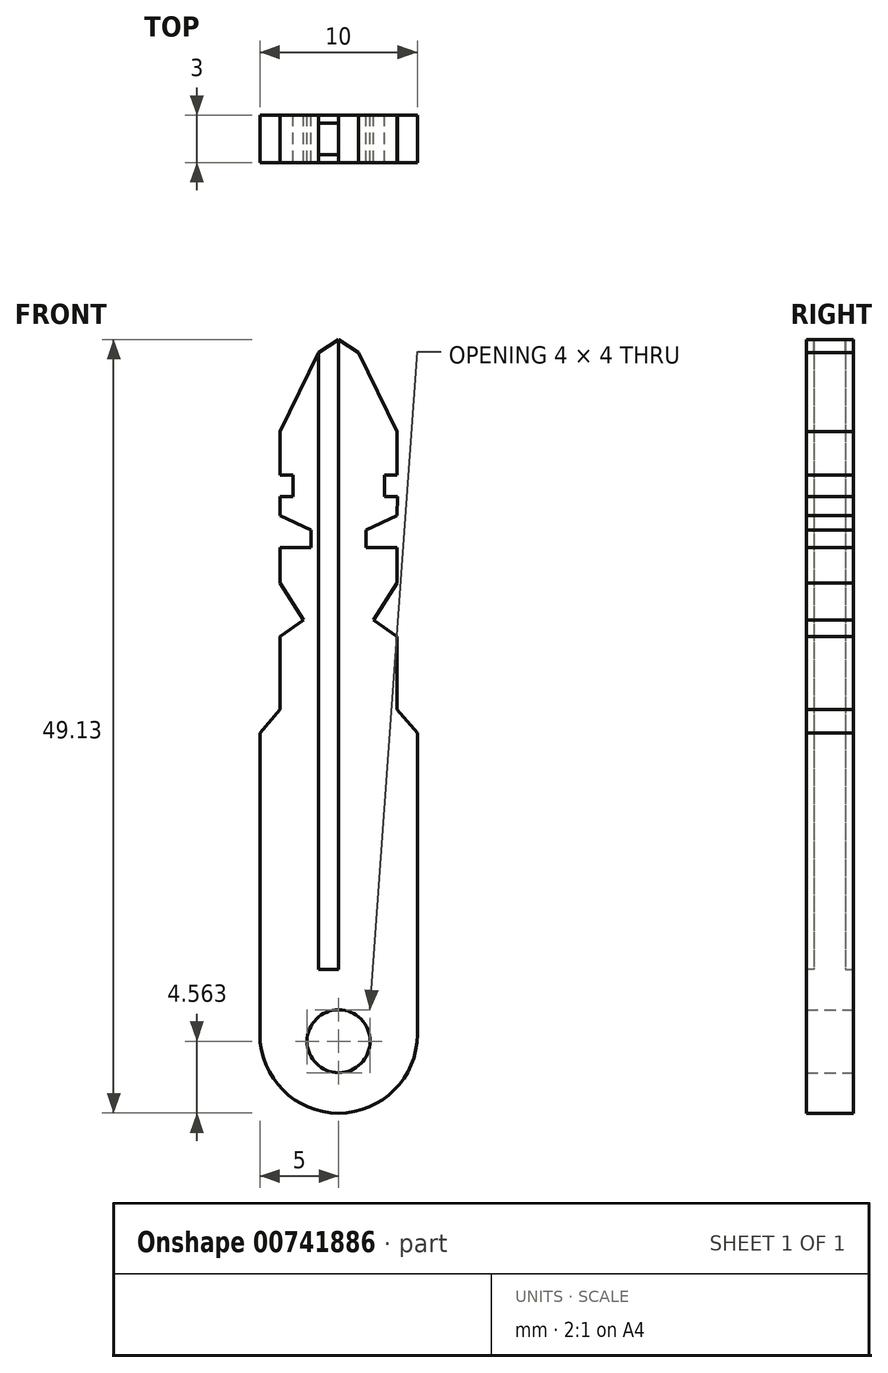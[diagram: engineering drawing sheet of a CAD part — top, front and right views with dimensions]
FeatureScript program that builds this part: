
annotation { "Feature Type Name" : "Feature", "Feature Type Description" : "" }
export const myFeature = defineFeature(function(context is Context, id is Id, definition is map)
    precondition{}
    {
        {
            var Q0;
            Q0=qCreatedBy(makeId("Front.planeOp"),FACE);
            var sketch = newSketch(context, id + "F0", { "sketchPlane" : qUnion([Q0])});
            skLineSegment(sketch, "E0", {"start": v(0, 0) * mm, "end": v(5, 0) * mm});
            skLineSegment(sketch, "E1", {"start": v(5, 0) * mm, "end": v(5, 15) * mm});
            skLineSegment(sketch, "E2", {"start": v(5, 15) * mm, "end": v(3.71, 16.5) * mm});
            skLineSegment(sketch, "E3", {"start": v(3.71, 16.5) * mm, "end": v(3.71, 21.14) * mm});
            skLineSegment(sketch, "E4", {"start": v(3.71, 21.14) * mm, "end": v(2.21, 22.18) * mm});
            skLineSegment(sketch, "E5", {"start": v(2.21, 22.18) * mm, "end": v(3.71, 24.53) * mm});
            skLineSegment(sketch, "E6", {"start": v(3.71, 24.53) * mm, "end": v(3.71, 26.79) * mm});
            skLineSegment(sketch, "E7", {"start": v(3.71, 26.79) * mm, "end": v(1.75, 26.79) * mm});
            skLineSegment(sketch, "E8", {"start": v(1.75, 26.79) * mm, "end": v(1.75, 27.89) * mm});
            skLineSegment(sketch, "E9", {"start": v(1.75, 27.89) * mm, "end": v(3.71, 28.82) * mm});
            skLineSegment(sketch, "E10", {"start": v(3.71, 28.82) * mm, "end": v(3.73, 30.03) * mm});
            skLineSegment(sketch, "E11", {"start": v(3.73, 30.03) * mm, "end": v(2.9, 30.04) * mm});
            skLineSegment(sketch, "E12", {"start": v(2.9, 30.04) * mm, "end": v(2.9, 31.4) * mm});
            skLineSegment(sketch, "E13", {"start": v(2.9, 31.4) * mm, "end": v(3.71, 31.4) * mm});
            skLineSegment(sketch, "E14", {"start": v(3.71, 31.4) * mm, "end": v(3.71, 34.16) * mm});
            skLineSegment(sketch, "E15", {"start": v(3.71, 34.16) * mm, "end": v(1.27, 39.19) * mm});
            skLineSegment(sketch, "E16", {"start": v(1.27, 39.19) * mm, "end": v(0, 40) * mm});
            skLineSegment(sketch, "E17.MirrorCS", {"start": v(-3.71, 34.16) * mm, "end": v(-1.27, 39.19) * mm});
            skLineSegment(sketch, "E18.MirrorCS", {"start": v(-3.71, 31.4) * mm, "end": v(-3.71, 34.16) * mm});
            skLineSegment(sketch, "E19.MirrorCS", {"start": v(-2.9, 30.04) * mm, "end": v(-2.9, 31.4) * mm});
            skLineSegment(sketch, "E20.MirrorCS", {"start": v(-3.73, 30.03) * mm, "end": v(-2.9, 30.04) * mm});
            skLineSegment(sketch, "E21.MirrorCS", {"start": v(-3.71, 28.82) * mm, "end": v(-3.73, 30.03) * mm});
            skLineSegment(sketch, "E22.MirrorCS", {"start": v(-1.75, 27.89) * mm, "end": v(-3.71, 28.82) * mm});
            skLineSegment(sketch, "E23.MirrorCS", {"start": v(-3.71, 26.79) * mm, "end": v(-1.75, 26.79) * mm});
            skLineSegment(sketch, "E24.MirrorCS", {"start": v(-3.71, 24.53) * mm, "end": v(-3.71, 26.79) * mm});
            skLineSegment(sketch, "E25.MirrorCS", {"start": v(-3.71, 21.14) * mm, "end": v(-2.21, 22.18) * mm});
            skLineSegment(sketch, "E26.MirrorCS", {"start": v(-2.21, 22.18) * mm, "end": v(-3.71, 24.53) * mm});
            skLineSegment(sketch, "E27.MirrorCS", {"start": v(-5, 15) * mm, "end": v(-3.71, 16.5) * mm});
            skLineSegment(sketch, "E28.MirrorCS", {"start": v(-3.71, 16.5) * mm, "end": v(-3.71, 21.14) * mm});
            skLineSegment(sketch, "E29.MirrorCS", {"start": v(-5, 0) * mm, "end": v(-5, 15) * mm});
            skLineSegment(sketch, "E30.MirrorCS", {"start": v(-1.27, 39.19) * mm, "end": v(0, 40) * mm});
            skLineSegment(sketch, "E31", {"start": v(-1.27, 39.19) * mm, "end": v(-1.27, 0) * mm});
            skLineSegment(sketch, "E32", {"start": v(-1.27, 0) * mm, "end": v(0, 0) * mm});
            skLineSegment(sketch, "E33", {"start": v(0, 40) * mm, "end": v(0, 0) * mm});
            skLineSegment(sketch, "E34", {"start": v(-5, 0) * mm, "end": v(0, 0) * mm});
            skLineSegment(sketch, "E35", {"start": v(-2.9, 31.4) * mm, "end": v(-3.71, 31.4) * mm});
            skLineSegment(sketch, "E36", {"start": v(-1.75, 26.79) * mm, "end": v(-1.75, 27.89) * mm});
            skSolve(sketch);
        }
        {
            var Q0;
            Q0 = qSketchRegion(id + "F0", true);
            extrude(context, id + "F1", {"entities" : qUnion([Q0]), "endBound" : BoundingType.SYMMETRIC, "depth" : 3 * mm, "offsetDistance" : 25 * mm});
        }
        {
            var Q0;
            Q0=makeQuery(id+"F1.opExtrude","CAP_FACE",FACE,{"disambiguationData":[OSD([sQuery(id+"F0.wireOp",EDGE,"E0"),sQuery(id+"F0.wireOp",EDGE,"E1"),sQuery(id+"F0.wireOp",EDGE,"E2"),sQuery(id+"F0.wireOp",EDGE,"E3"),sQuery(id+"F0.wireOp",EDGE,"E4"),sQuery(id+"F0.wireOp",EDGE,"E5"),sQuery(id+"F0.wireOp",EDGE,"E6"),sQuery(id+"F0.wireOp",EDGE,"E7"),sQuery(id+"F0.wireOp",EDGE,"E8"),sQuery(id+"F0.wireOp",EDGE,"E9"),sQuery(id+"F0.wireOp",EDGE,"E10"),sQuery(id+"F0.wireOp",EDGE,"E11"),sQuery(id+"F0.wireOp",EDGE,"E12"),sQuery(id+"F0.wireOp",EDGE,"E13"),sQuery(id+"F0.wireOp",EDGE,"E14"),sQuery(id+"F0.wireOp",EDGE,"E15"),sQuery(id+"F0.wireOp",EDGE,"E16"),sQuery(id+"F0.wireOp",EDGE,"E17.MirrorCS"),sQuery(id+"F0.wireOp",EDGE,"E18.MirrorCS"),sQuery(id+"F0.wireOp",EDGE,"E19.MirrorCS"),sQuery(id+"F0.wireOp",EDGE,"E20.MirrorCS"),sQuery(id+"F0.wireOp",EDGE,"E21.MirrorCS"),sQuery(id+"F0.wireOp",EDGE,"E22.MirrorCS"),sQuery(id+"F0.wireOp",EDGE,"E23.MirrorCS"),sQuery(id+"F0.wireOp",EDGE,"E24.MirrorCS"),sQuery(id+"F0.wireOp",EDGE,"E25.MirrorCS"),sQuery(id+"F0.wireOp",EDGE,"E26.MirrorCS"),sQuery(id+"F0.wireOp",EDGE,"E27.MirrorCS"),sQuery(id+"F0.wireOp",EDGE,"E28.MirrorCS"),sQuery(id+"F0.wireOp",EDGE,"E29.MirrorCS"),sQuery(id+"F0.wireOp",EDGE,"E30.MirrorCS"),sQuery(id+"F0.wireOp",EDGE,"E34"),sQuery(id+"F0.wireOp",EDGE,"E35"),sQuery(id+"F0.wireOp",EDGE,"E36")])],"isStart":false});
            var sketch = newSketch(context, id + "F2", { "sketchPlane" : qUnion([Q0])});
            skLineSegment(sketch, "E37.0", {"start": v(0, 40) * mm, "end": v(0, 0) * mm});
            skLineSegment(sketch, "E38.0", {"start": v(-1.27, 39.19) * mm, "end": v(-1.27, 0) * mm});
            skLineSegment(sketch, "E39.0", {"start": v(-1.27, 0) * mm, "end": v(0, 0) * mm});
            skPoint(sketch, "E40.orphan", {"position": v(-5, 0) * mm});
            skPoint(sketch, "E41.orphan", {"position": v(-1.27, 39.19) * mm});
            skPoint(sketch, "E42.0.end.orphan", {"position": v(0, 40) * mm});
            skLineSegment(sketch, "E43.0", {"start": v(-1.27, 39.19) * mm, "end": v(0, 40) * mm});
            skSolve(sketch);
        }
        {
            var Q0;
            Q0 = qSketchRegion(id + "F2", true);
            extrude(context, id + "F3", {"entities" : qUnion([Q0]), "operationType" : NewBodyOperationType.REMOVE, "oppositeDirection" : true, "depth" : .5 * mm, "offsetDistance" : 25 * mm});
        }
        {
            var Q0;
            Q0=makeQuery(id+"F1.opExtrude","CAP_FACE",FACE,{"disambiguationData":[OSD([sQuery(id+"F0.wireOp",EDGE,"E0"),sQuery(id+"F0.wireOp",EDGE,"E1"),sQuery(id+"F0.wireOp",EDGE,"E2"),sQuery(id+"F0.wireOp",EDGE,"E3"),sQuery(id+"F0.wireOp",EDGE,"E4"),sQuery(id+"F0.wireOp",EDGE,"E5"),sQuery(id+"F0.wireOp",EDGE,"E6"),sQuery(id+"F0.wireOp",EDGE,"E7"),sQuery(id+"F0.wireOp",EDGE,"E8"),sQuery(id+"F0.wireOp",EDGE,"E9"),sQuery(id+"F0.wireOp",EDGE,"E10"),sQuery(id+"F0.wireOp",EDGE,"E11"),sQuery(id+"F0.wireOp",EDGE,"E12"),sQuery(id+"F0.wireOp",EDGE,"E13"),sQuery(id+"F0.wireOp",EDGE,"E14"),sQuery(id+"F0.wireOp",EDGE,"E15"),sQuery(id+"F0.wireOp",EDGE,"E16"),sQuery(id+"F0.wireOp",EDGE,"E17.MirrorCS"),sQuery(id+"F0.wireOp",EDGE,"E18.MirrorCS"),sQuery(id+"F0.wireOp",EDGE,"E19.MirrorCS"),sQuery(id+"F0.wireOp",EDGE,"E20.MirrorCS"),sQuery(id+"F0.wireOp",EDGE,"E21.MirrorCS"),sQuery(id+"F0.wireOp",EDGE,"E22.MirrorCS"),sQuery(id+"F0.wireOp",EDGE,"E23.MirrorCS"),sQuery(id+"F0.wireOp",EDGE,"E24.MirrorCS"),sQuery(id+"F0.wireOp",EDGE,"E25.MirrorCS"),sQuery(id+"F0.wireOp",EDGE,"E26.MirrorCS"),sQuery(id+"F0.wireOp",EDGE,"E27.MirrorCS"),sQuery(id+"F0.wireOp",EDGE,"E28.MirrorCS"),sQuery(id+"F0.wireOp",EDGE,"E29.MirrorCS"),sQuery(id+"F0.wireOp",EDGE,"E30.MirrorCS"),sQuery(id+"F0.wireOp",EDGE,"E34"),sQuery(id+"F0.wireOp",EDGE,"E35"),sQuery(id+"F0.wireOp",EDGE,"E36")])],"isStart":true});
            var sketch = newSketch(context, id + "F4", { "sketchPlane" : qUnion([Q0])});
            skLineSegment(sketch, "E44.0", {"start": v(1.27, 39.19) * mm, "end": v(1.27, 0) * mm});
            skLineSegment(sketch, "E45.0", {"start": v(0, 40) * mm, "end": v(0, 0) * mm});
            skLineSegment(sketch, "E46.0", {"start": v(1.27, 39.19) * mm, "end": v(0, 40) * mm});
            skLineSegment(sketch, "E47.0", {"start": v(1.27, 0) * mm, "end": v(0, 0) * mm});
            skPoint(sketch, "E48.orphan", {"position": v(5, 0) * mm});
            skSolve(sketch);
        }
        {
            var Q0;
            Q0 = qSketchRegion(id + "F4", true);
            extrude(context, id + "F5", {"entities" : qUnion([Q0]), "operationType" : NewBodyOperationType.REMOVE, "oppositeDirection" : true, "depth" : .5 * mm, "offsetDistance" : 25 * mm});
        }
        {
            var Q0;
            {var subQ0=sQuery(id+"F0.wireOp",EDGE,"E9");var subQ1=sQuery(id+"F0.wireOp",EDGE,"E8");var subQ2=sQuery(id+"F0.wireOp",EDGE,"E7");var subQ3=sQuery(id+"F0.wireOp",EDGE,"E6");var subQ4=sQuery(id+"F0.wireOp",EDGE,"E5");var subQ5=sQuery(id+"F0.wireOp",EDGE,"E4");var subQ6=sQuery(id+"F0.wireOp",EDGE,"E34");var subQ7=sQuery(id+"F0.wireOp",EDGE,"E0");var subQ8=sQuery(id+"F0.wireOp",EDGE,"E1");var subQ9=sQuery(id+"F0.wireOp",EDGE,"E2");var subQ10=sQuery(id+"F0.wireOp",EDGE,"E3");var subQ11=sQuery(id+"F0.wireOp",EDGE,"E10");var subQ12=sQuery(id+"F0.wireOp",EDGE,"E11");var subQ13=sQuery(id+"F0.wireOp",EDGE,"E12");var subQ14=sQuery(id+"F0.wireOp",EDGE,"E13");var subQ15=sQuery(id+"F0.wireOp",EDGE,"E14");var subQ16=sQuery(id+"F0.wireOp",EDGE,"E15");var subQ17=sQuery(id+"F0.wireOp",EDGE,"E16");Q0=makeQuery(id+"F5.boolean.opBoolean","SPLIT",FACE,{"disambiguationData":[TD([makeQuery(id+"F1.opExtrude","SWEPT_FACE",FACE,{"disambiguationData":[OSD([subQ8])]})])],"derivedFrom":makeQuery(id+"F1.opExtrude","CAP_FACE",FACE,{"disambiguationData":[OSD([subQ7,subQ8,subQ9,subQ10,subQ5,subQ4,subQ3,subQ2,subQ1,subQ0,subQ11,subQ12,subQ13,subQ14,subQ15,subQ16,subQ17,sQuery(id+"F0.wireOp",EDGE,"E17.MirrorCS"),sQuery(id+"F0.wireOp",EDGE,"E18.MirrorCS"),sQuery(id+"F0.wireOp",EDGE,"E19.MirrorCS"),sQuery(id+"F0.wireOp",EDGE,"E20.MirrorCS"),sQuery(id+"F0.wireOp",EDGE,"E21.MirrorCS"),sQuery(id+"F0.wireOp",EDGE,"E22.MirrorCS"),sQuery(id+"F0.wireOp",EDGE,"E23.MirrorCS"),sQuery(id+"F0.wireOp",EDGE,"E24.MirrorCS"),sQuery(id+"F0.wireOp",EDGE,"E25.MirrorCS"),sQuery(id+"F0.wireOp",EDGE,"E26.MirrorCS"),sQuery(id+"F0.wireOp",EDGE,"E27.MirrorCS"),sQuery(id+"F0.wireOp",EDGE,"E28.MirrorCS"),sQuery(id+"F0.wireOp",EDGE,"E29.MirrorCS"),sQuery(id+"F0.wireOp",EDGE,"E30.MirrorCS"),subQ6,sQuery(id+"F0.wireOp",EDGE,"E35"),sQuery(id+"F0.wireOp",EDGE,"E36")])],"isStart":true})});}
            var sketch = newSketch(context, id + "F6", { "sketchPlane" : qUnion([Q0])});
            skLineSegment(sketch, "E49", {"start": v(-5, -4.13) * mm, "end": v(-5, 0) * mm});
            skLineSegment(sketch, "E50", {"start": v(0, 0) * mm, "end": v(-5, 0) * mm});
            skPoint(sketch, "E51.orphan", {"position": v(0, 0) * mm});
            skLineSegment(sketch, "E52", {"start": v(-5, 0) * mm, "end": v(5, 0) * mm});
            skLineSegment(sketch, "E53", {"start": v(5, 0) * mm, "end": v(5, -4.13) * mm});
            skLineSegment(sketch, "E54", {"start": v(0, -9.13) * mm, "end": v(0, -9.13) * mm});
            skLineSegment(sketch, "E55", {"start": v(0, 0) * mm, "end": v(0, -9.13) * mm});
            skCircle(sketch, "E56", {"center": v(0, -4.57) * mm, "radius": 2 * mm});
            skPoint(sketch, "E57.visualSharp", {"position": v(-5, -9.13) * mm});
            skArc(sketch, "E57.filletArc", {"start": v(-5, -4.13) * mm, "mid": v(-3.54, -7.67) * mm, "end": v(0, -9.13) * mm});
            skPoint(sketch, "E58.visualSharp", {"position": v(5, -9.13) * mm});
            skArc(sketch, "E58.filletArc", {"start": v(0, -9.13) * mm, "mid": v(3.54, -7.67) * mm, "end": v(5, -4.13) * mm});
            skLineSegment(sketch, "E59.0", {"start": v(0, 40) * mm, "end": v(0, 0) * mm});
            skLineSegment(sketch, "E60", {"start": v(0, -6.57) * mm, "end": v(0, -9.13) * mm});
            skSolve(sketch);
        }
        {
            var Q0;
            {var subQ3=sQuery(id+"F6.wireOp",EDGE,"Q4FwNhOH-Ctd4-7uqG-ik7L-jfaRsiHFqxHk");Q0=makeQuery(id+"F6.imprint","IMPRINT",FACE,{"disambiguationData":[TD([[makeQuery(id+"F6.imprint","IMPRINT",EDGE,{"derivedFrom":subQ3}),-1.0]])]});}
            var Q1;
            {var subQ6=sQuery(id+"F6.wireOp",EDGE,"E49");Q1=makeQuery(id+"F6.imprint","IMPRINT",FACE,{"disambiguationData":[TD([[makeQuery(id+"F6.imprint","IMPRINT",EDGE,{"derivedFrom":subQ6}),-1.0]])]});}
            var Q2;
            {var subQ6=sQuery(id+"F6.wireOp",EDGE,"E53");Q2=makeQuery(id+"F6.imprint","IMPRINT",FACE,{"disambiguationData":[TD([[makeQuery(id+"F6.imprint","IMPRINT",EDGE,{"derivedFrom":subQ6}),-1.0]])]});}
            extrude(context, id + "F7", {"entities" : qUnion([Q0, Q1, Q2]), "operationType" : NewBodyOperationType.ADD, "oppositeDirection" : true, "depth" : 3 * mm, "offsetDistance" : 25 * mm});
        }
    });
